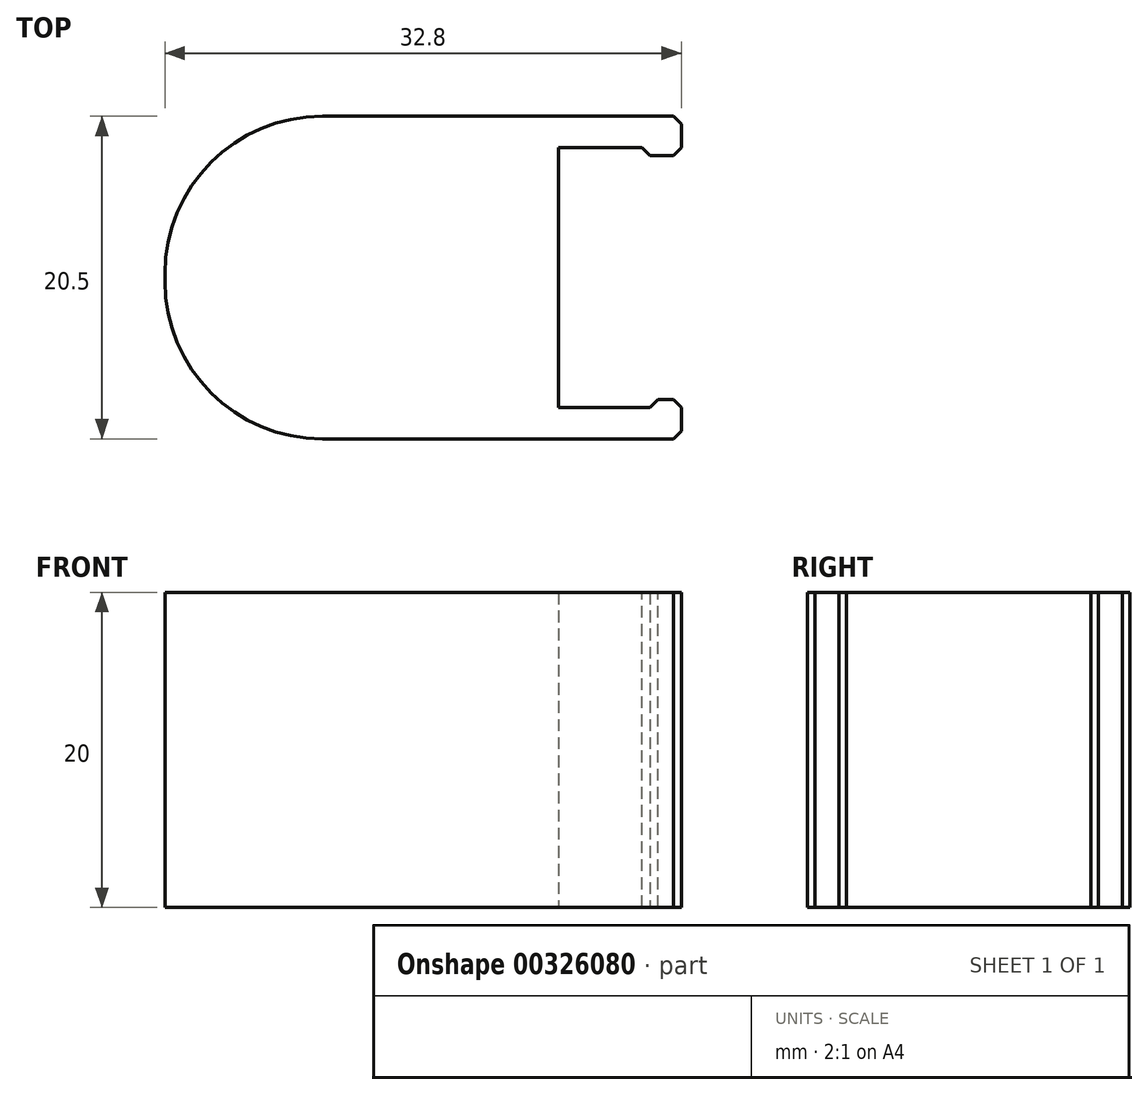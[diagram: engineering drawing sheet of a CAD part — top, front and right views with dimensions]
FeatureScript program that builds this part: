
annotation { "Feature Type Name" : "Feature", "Feature Type Description" : "" }
export const myFeature = defineFeature(function(context is Context, id is Id, definition is map)
    precondition{}
    {
        {
            var Q0;
            Q0=qCreatedBy(makeId("Top.planeOp"),FACE);
            var sketch = newSketch(context, id + "F0", { "sketchPlane" : qUnion([Q0])});
            skLineSegment(sketch, "E0.bottom", {"start": v(-42.8, 47.35) * mm, "end": v(-37, 47.35) * mm});
            skLineSegment(sketch, "E0.top", {"start": v(-42.8, 45.35) * mm, "end": v(-37, 45.35) * mm});
            skLineSegment(sketch, "E0.left", {"start": v(-42.8, 47.35) * mm, "end": v(-42.8, 45.35) * mm});
            skLineSegment(sketch, "E0.right", {"start": v(-37, 47.35) * mm, "end": v(-37, 45.35) * mm});
            skLineSegment(sketch, "E1.bottom", {"start": v(-42.8, 28.85) * mm, "end": v(-37, 28.85) * mm});
            skLineSegment(sketch, "E1.top", {"start": v(-42.8, 26.85) * mm, "end": v(-37, 26.85) * mm});
            skLineSegment(sketch, "E1.left", {"start": v(-42.8, 28.85) * mm, "end": v(-42.8, 26.85) * mm});
            skLineSegment(sketch, "E1.right", {"start": v(-37, 28.85) * mm, "end": v(-37, 26.85) * mm});
            skLineSegment(sketch, "E2.bottom", {"start": v(-42.8, 47.35) * mm, "end": v(-67.8, 47.35) * mm});
            skLineSegment(sketch, "E2.top", {"start": v(-42.8, 26.85) * mm, "end": v(-67.8, 26.85) * mm});
            skLineSegment(sketch, "E2.left", {"start": v(-42.8, 47.35) * mm, "end": v(-42.8, 26.85) * mm});
            skLineSegment(sketch, "E2.right", {"start": v(-67.8, 47.35) * mm, "end": v(-67.8, 26.85) * mm});
            skLineSegment(sketch, "E3.bottom", {"start": v(-37, 47.35) * mm, "end": v(-35, 47.35) * mm});
            skLineSegment(sketch, "E3.top", {"start": v(-37, 44.85) * mm, "end": v(-35, 44.85) * mm});
            skLineSegment(sketch, "E3.left", {"start": v(-37, 47.35) * mm, "end": v(-37, 44.85) * mm});
            skLineSegment(sketch, "E3.right", {"start": v(-35, 47.35) * mm, "end": v(-35, 44.85) * mm});
            skLineSegment(sketch, "E4.bottom", {"start": v(-37, 26.85) * mm, "end": v(-35, 26.85) * mm});
            skLineSegment(sketch, "E4.top", {"start": v(-37, 29.35) * mm, "end": v(-35, 29.35) * mm});
            skLineSegment(sketch, "E4.left", {"start": v(-37, 26.85) * mm, "end": v(-37, 29.35) * mm});
            skLineSegment(sketch, "E4.right", {"start": v(-35, 26.85) * mm, "end": v(-35, 29.35) * mm});
            skSolve(sketch);
        }
        {
            var Q0;
            Q0=qSketchRegion(id+"F0",true);
            extrude(context, id + "F1", {"entities" : qUnion([Q0]), "depth" : 20 * mm});
        }
        {
            var Q0;
            Q0=makeQuery(id+"F1.opExtrude","SWEPT_EDGE",EDGE,{"disambiguationData":[OSD([sQuery(id+"F0.wireOp",EDGE,"E2.bottom"),sQuery(id+"F0.wireOp",EDGE,"E2.right")])]});
            var Q1;
            Q1=makeQuery(id+"F1.opExtrude","SWEPT_EDGE",EDGE,{"disambiguationData":[OSD([sQuery(id+"F0.wireOp",EDGE,"E2.top"),sQuery(id+"F0.wireOp",EDGE,"E2.right")])]});
            fillet(context, id + "F2", {"entities" : qUnion([Q0, Q1]), "radius" : 10 * mm, "tangentPropagation" : true, "allowEdgeOverflow" : false});
        }
        {
            var Q0;
            Q0=makeQuery(id+"F1.opExtrude","SWEPT_EDGE",EDGE,{"disambiguationData":[OSD([sQuery(id+"F0.wireOp",EDGE,"E3.bottom"),sQuery(id+"F0.wireOp",EDGE,"E3.right")])]});
            var Q1;
            Q1=makeQuery(id+"F1.opExtrude","SWEPT_EDGE",EDGE,{"disambiguationData":[OSD([sQuery(id+"F0.wireOp",EDGE,"E3.top"),sQuery(id+"F0.wireOp",EDGE,"E3.right")])]});
            var Q2;
            Q2=makeQuery(id+"F1.opExtrude","SWEPT_EDGE",EDGE,{"disambiguationData":[OSD([sQuery(id+"F0.wireOp",EDGE,"E4.top"),sQuery(id+"F0.wireOp",EDGE,"E4.right")])]});
            var Q3;
            Q3=makeQuery(id+"F1.opExtrude","SWEPT_EDGE",EDGE,{"disambiguationData":[OSD([sQuery(id+"F0.wireOp",EDGE,"E4.bottom"),sQuery(id+"F0.wireOp",EDGE,"E4.right")])]});
            var Q4;
            Q4=makeQuery(id+"F1.opExtrude","SWEPT_EDGE",EDGE,{"disambiguationData":[OSD([sQuery(id+"F0.wireOp",EDGE,"E4.top"),sQuery(id+"F0.wireOp",EDGE,"E4.left")])]});
            var Q5;
            Q5=makeQuery(id+"F1.opExtrude","SWEPT_EDGE",EDGE,{"disambiguationData":[OSD([sQuery(id+"F0.wireOp",EDGE,"E0.top"),sQuery(id+"F0.wireOp",EDGE,"E3.left")])]});
            chamfer(context, id + "F3", {"entities" : qUnion([Q0, Q1, Q2, Q3, Q4, Q5]), "width" : .5 * mm, "tangentPropagation" : true});
        }
    });
